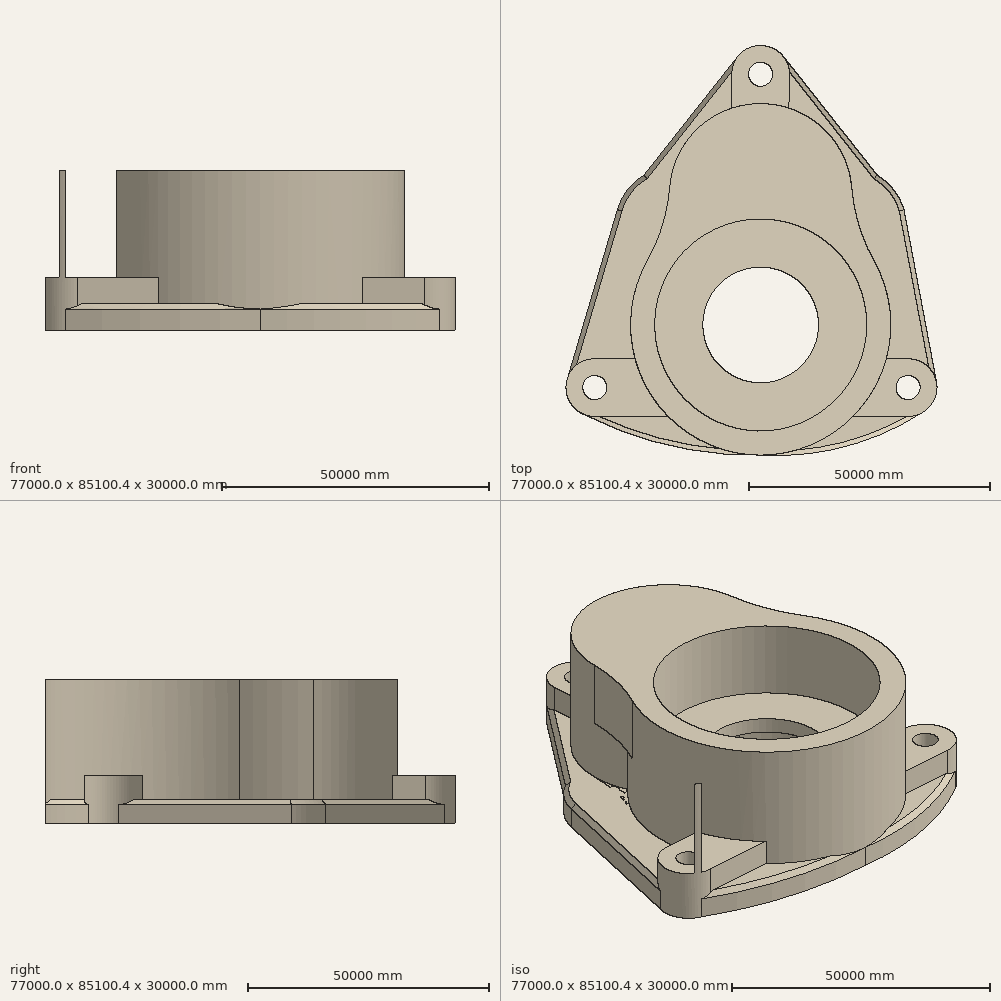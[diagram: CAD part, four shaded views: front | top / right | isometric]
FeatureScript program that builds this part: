
annotation { "Feature Type Name" : "Feature", "Feature Type Description" : "" }
export const myFeature = defineFeature(function(context is Context, id is Id, definition is map)
    precondition{}
    {
        {
            var Q0;
            Q0=qCreatedBy(makeId("Top.planeOp"),FACE);
            var sketch = newSketch(context, id + "F0", { "sketchPlane" : qUnion([Q0])});
            skCircle(sketch, "E0", {"center": v(0, 0) * mm, "radius": 27000 * mm});
            skCircle(sketch, "E1", {"center": v(0, 0) * mm, "radius": 22000 * mm});
            skCircle(sketch, "E2", {"center": v(0, 0) * mm, "radius": 12000 * mm});
            skCircle(sketch, "E3", {"center": v(0, 27000) * mm, "radius": 13939.8 * mm});
            skArc(sketch, "E4", {"start": v(17736.64, 20357.1) * mm, "mid": v(0, 45939.8) * mm, "end": v(-17736.64, 20357.1) * mm});
            skCircle(sketch, "E5", {"center": v(0, 52000) * mm, "radius": 6000 * mm});
            skCircle(sketch, "E6", {"center": v(0, 52000) * mm, "radius": 2500 * mm});
            skLineSegment(sketch, "E7", {"start": v(-5996.4, 52208) * mm, "end": v(-5996.4, 44965.51) * mm});
            skLineSegment(sketch, "E8", {"start": v(5998.36, 51859.79) * mm, "end": v(5838.42, 45017.47) * mm});
            skCircle(sketch, "E9", {"center": v(-34415.2, -13000) * mm, "radius": 2500 * mm});
            skCircle(sketch, "E10", {"center": v(30584.8, -13000) * mm, "radius": 2500 * mm});
            skCircle(sketch, "E11", {"center": v(-34415.2, -13000) * mm, "radius": 6000 * mm});
            skCircle(sketch, "E12", {"center": v(30584.8, -13000) * mm, "radius": 6000 * mm});
            skLineSegment(sketch, "E13", {"start": v(-34341.66, -18999.55) * mm, "end": v(-19183.77, -18999.55) * mm});
            skLineSegment(sketch, "E14", {"start": v(-34415.2, -7000) * mm, "end": v(-26076.8, -7000) * mm});
            skLineSegment(sketch, "E15", {"start": v(30695.67, -18998.98) * mm, "end": v(19184.34, -18998.98) * mm});
            skLineSegment(sketch, "E16", {"start": v(30584.8, -7000) * mm, "end": v(26076.8, -7000) * mm});
            skPoint(sketch, "E17", {"position": v(-28142.5, 27000) * mm});
            skPoint(sketch, "E18", {"position": v(28142.5, 27000) * mm});
            skArc(sketch, "E19", {"start": v(-24201.45, 31055.53) * mm, "mid": v(-27631.17, 27995.7) * mm, "end": v(-29723.12, 23903.13) * mm});
            skArc(sketch, "E20", {"start": v(30190.87, 21425.74) * mm, "mid": v(28351.05, 26958.94) * mm, "end": v(24201.45, 31055.53) * mm});
            skLineSegment(sketch, "E21", {"start": v(-39967.73, -10726.37) * mm, "end": v(-29723.12, 23903.13) * mm});
            skLineSegment(sketch, "E22", {"start": v(-24201.45, 31055.53) * mm, "end": v(-4707.26, 55720.44) * mm});
            skLineSegment(sketch, "E23", {"start": v(36480.63, -11886.8) * mm, "end": v(29723.12, 23903.13) * mm});
            skLineSegment(sketch, "E24", {"start": v(24201.45, 31055.53) * mm, "end": v(4707.26, 55720.44) * mm});
            skArc(sketch, "E25", {"start": v(-37734.14, -17998.46) * mm, "mid": v(-19439.08, -24897.08) * mm, "end": v(0, -27000) * mm});
            skArc(sketch, "E26", {"start": v(0, -27000) * mm, "mid": v(17495.5, -25276.65) * mm, "end": v(33586.38, -18195.24) * mm});
            skPoint(sketch, "E27.orphan", {"position": v(-40311.03, -11886.8) * mm});
            skSolve(sketch);
        }
        {
            var Q0;
            {var subQ0=sQuery(id+"F0.wireOp",EDGE,"E25");var subQ1=sQuery(id+"F0.wireOp",EDGE,"E11");var subQ2=makeQuery(id+"F0.imprint","INTERSECT",VERTEX,{"disambiguationData":[OD(0.0)],"derivedFrom":[subQ1,subQ0]});Q0=makeQuery(id+"F0.imprint","IMPRINT",FACE,{"disambiguationData":[TD([[makeQuery(id+"F0.imprint","IMPRINT",EDGE,{"disambiguationData":[TD([[subQ2,-1.0]])],"derivedFrom":subQ1}),1.0]])]});}
            var Q1;
            {var subQ0=sQuery(id+"F0.wireOp",EDGE,"E23");var subQ1=sQuery(id+"F0.wireOp",EDGE,"E20");var subQ2=makeQuery(id+"F0.imprint","INTERSECT",VERTEX,{"disambiguationData":[OD(0.0)],"derivedFrom":[subQ1,subQ0]});Q1=makeQuery(id+"F0.imprint","IMPRINT",FACE,{"disambiguationData":[TD([[makeQuery(id+"F0.imprint","IMPRINT",EDGE,{"disambiguationData":[TD([[subQ2,-1.0]])],"derivedFrom":subQ1}),1.0]])]});}
            var Q2;
            {var subQ0=sQuery(id+"F0.wireOp",EDGE,"E4");var subQ1=sQuery(id+"F0.wireOp",EDGE,"E0");var subQ2=makeQuery(id+"F0.imprint","INTERSECT",VERTEX,{"disambiguationData":[OD(0.0)],"derivedFrom":[subQ1,subQ0]});Q2=makeQuery(id+"F0.imprint","IMPRINT",FACE,{"disambiguationData":[TD([[makeQuery(id+"F0.imprint","IMPRINT",EDGE,{"disambiguationData":[TD([[subQ2,-1.0]])],"derivedFrom":subQ1}),-1.0]])]});}
            var Q3;
            {var subQ0=sQuery(id+"F0.wireOp",EDGE,"E3");var subQ1=sQuery(id+"F0.wireOp",EDGE,"E0");var subQ2=makeQuery(id+"F0.imprint","INTERSECT",VERTEX,{"disambiguationData":[OD(0.0)],"derivedFrom":[subQ1,subQ0]});Q3=makeQuery(id+"F0.imprint","IMPRINT",FACE,{"disambiguationData":[TD([[makeQuery(id+"F0.imprint","IMPRINT",EDGE,{"disambiguationData":[TD([[subQ2,-1.0]])],"derivedFrom":subQ1}),-1.0]])]});}
            var Q4;
            {var subQ0=sQuery(id+"F0.wireOp",EDGE,"E3");var subQ1=sQuery(id+"F0.wireOp",EDGE,"E0");var subQ2=makeQuery(id+"F0.imprint","INTERSECT",VERTEX,{"disambiguationData":[OD(0.0)],"derivedFrom":[subQ1,subQ0]});Q4=makeQuery(id+"F0.imprint","IMPRINT",FACE,{"disambiguationData":[TD([[makeQuery(id+"F0.imprint","IMPRINT",EDGE,{"disambiguationData":[TD([[subQ2,-1.0]])],"derivedFrom":subQ1}),1.0]])]});}
            var Q5;
            {var subQ0=sQuery(id+"F0.wireOp",EDGE,"E3");var subQ1=sQuery(id+"F0.wireOp",EDGE,"E1");var subQ2=makeQuery(id+"F0.imprint","INTERSECT",VERTEX,{"disambiguationData":[OD(0.0)],"derivedFrom":[subQ1,subQ0]});Q5=makeQuery(id+"F0.imprint","IMPRINT",FACE,{"disambiguationData":[TD([[makeQuery(id+"F0.imprint","IMPRINT",EDGE,{"disambiguationData":[TD([[subQ2,1.0]])],"derivedFrom":subQ1}),1.0]])]});}
            var Q6;
            {var subQ1=sQuery(id+"F0.wireOp",EDGE,"E0");var subQ6=sQuery(id+"F0.wireOp",EDGE,"E4");var subQ7=makeQuery(id+"F0.imprint","INTERSECT",VERTEX,{"disambiguationData":[OD(0.0)],"derivedFrom":[subQ1,subQ6]});Q6=makeQuery(id+"F0.imprint","IMPRINT",FACE,{"disambiguationData":[TD([[makeQuery(id+"F0.imprint","IMPRINT",EDGE,{"disambiguationData":[TD([[subQ7,-1.0]])],"derivedFrom":subQ1}),1.0]])]});}
            var Q7;
            Q7=makeQuery(id+"F0.imprint","IMPRINT",FACE,{"disambiguationData":[TD([[makeQuery(id+"F0.imprint","IMPRINT",EDGE,{"derivedFrom":sQuery(id+"F0.wireOp",EDGE,"E2")}),1.0]])]});
            var Q8;
            Q8=makeQuery(id+"F0.imprint","IMPRINT",FACE,{"disambiguationData":[TD([[makeQuery(id+"F0.imprint","IMPRINT",EDGE,{"derivedFrom":sQuery(id+"F0.wireOp",EDGE,"E2")}),-1.0]])]});
            extrude(context, id + "F1", {"entities" : qUnion([Q0, Q1, Q2, Q3, Q4, Q5, Q6, Q7, Q8]), "depth" : 30000 * mm});
        }
        {
            var Q0;
            {var subQ0=sQuery(id+"F0.wireOp",EDGE,"E4");var subQ1=sQuery(id+"F0.wireOp",EDGE,"E0");Q0=makeQuery(id+"F1.opExtrude","SWEPT_EDGE",EDGE,{"disambiguationData":[OSD([subQ1,subQ0]),TDD([makeQuery(id+"F0.imprint","INTERSECT",VERTEX,{"disambiguationData":[OD(0.0)],"derivedFrom":[subQ1,subQ0]})])]});}
            var Q1;
            {var subQ0=sQuery(id+"F0.wireOp",EDGE,"E4");var subQ1=sQuery(id+"F0.wireOp",EDGE,"E0");Q1=makeQuery(id+"F1.opExtrude","SWEPT_EDGE",EDGE,{"disambiguationData":[OSD([subQ1,subQ0]),TDD([makeQuery(id+"F0.imprint","INTERSECT",VERTEX,{"disambiguationData":[OD(1.0)],"derivedFrom":[subQ1,subQ0]})])]});}
            fillet(context, id + "F2", {"entities" : qUnion([Q0, Q1]), "radius" : 37817.8 * mm, "tangentPropagation" : true, "allowEdgeOverflow" : false});
        }
        {
            var Q0;
            Q0=makeQuery(id+"F0.imprint","IMPRINT",FACE,{"disambiguationData":[TD([[makeQuery(id+"F0.imprint","IMPRINT",EDGE,{"derivedFrom":sQuery(id+"F0.wireOp",EDGE,"E6")}),-1.0]])]});
            var Q1;
            {var subQ0=sQuery(id+"F0.wireOp",EDGE,"E7");var subQ1=sQuery(id+"F0.wireOp",EDGE,"E4");var subQ2=makeQuery(id+"F0.imprint","INTERSECT",VERTEX,{"derivedFrom":[subQ1,subQ0]});Q1=makeQuery(id+"F0.imprint","IMPRINT",FACE,{"disambiguationData":[TD([[makeQuery(id+"F0.imprint","IMPRINT",EDGE,{"disambiguationData":[TD([[subQ2,1.0]])],"derivedFrom":subQ1}),-1.0]])]});}
            var Q2;
            {var subQ0=sQuery(id+"F0.wireOp",EDGE,"E8");Q2=makeQuery(id+"F0.imprint","IMPRINT",FACE,{"disambiguationData":[TD([[makeQuery(id+"F0.imprint","IMPRINT",EDGE,{"derivedFrom":subQ0}),-1.0]])]});}
            var Q3;
            {var subQ3=sQuery(id+"F0.wireOp",EDGE,"E16");Q3=makeQuery(id+"F0.imprint","IMPRINT",FACE,{"disambiguationData":[TD([[makeQuery(id+"F0.imprint","IMPRINT",EDGE,{"derivedFrom":subQ3}),1.0]])]});}
            var Q4;
            Q4=makeQuery(id+"F0.imprint","IMPRINT",FACE,{"disambiguationData":[TD([[makeQuery(id+"F0.imprint","IMPRINT",EDGE,{"derivedFrom":sQuery(id+"F0.wireOp",EDGE,"E10")}),-1.0]])]});
            var Q5;
            Q5=makeQuery(id+"F0.imprint","IMPRINT",FACE,{"disambiguationData":[TD([[makeQuery(id+"F0.imprint","IMPRINT",EDGE,{"derivedFrom":sQuery(id+"F0.wireOp",EDGE,"E9")}),-1.0]])]});
            var Q6;
            {var subQ0=sQuery(id+"F0.wireOp",EDGE,"E13");Q6=makeQuery(id+"F0.imprint","IMPRINT",FACE,{"disambiguationData":[TD([[makeQuery(id+"F0.imprint","IMPRINT",EDGE,{"derivedFrom":subQ0}),1.0]])]});}
            extrude(context, id + "F3", {"entities" : qUnion([Q0, Q1, Q2, Q3, Q4, Q5, Q6]), "operationType" : NewBodyOperationType.ADD, "depth" : 10000 * mm});
        }
        {
            var Q0;
            {var subQ5=sQuery(id+"F0.wireOp",EDGE,"E14");Q0=makeQuery(id+"F0.imprint","IMPRINT",FACE,{"disambiguationData":[TD([[makeQuery(id+"F0.imprint","IMPRINT",EDGE,{"derivedFrom":subQ5}),1.0]])]});}
            var Q1;
            {var subQ0=sQuery(id+"F0.wireOp",EDGE,"E8");Q1=makeQuery(id+"F0.imprint","IMPRINT",FACE,{"disambiguationData":[TD([[makeQuery(id+"F0.imprint","IMPRINT",EDGE,{"derivedFrom":subQ0}),1.0]])]});}
            var Q2;
            {var subQ0=sQuery(id+"F0.wireOp",EDGE,"E13");Q2=makeQuery(id+"F0.imprint","IMPRINT",FACE,{"disambiguationData":[TD([[makeQuery(id+"F0.imprint","IMPRINT",EDGE,{"derivedFrom":subQ0}),-1.0]])]});}
            var Q3;
            {var subQ6=sQuery(id+"F0.wireOp",EDGE,"E26");Q3=makeQuery(id+"F0.imprint","IMPRINT",FACE,{"disambiguationData":[TD([[makeQuery(id+"F0.imprint","IMPRINT",EDGE,{"derivedFrom":subQ6}),1.0]])]});}
            extrude(context, id + "F4", {"entities" : qUnion([Q0, Q1, Q2, Q3]), "depth" : 5000 * mm});
        }
        {
            var Q0;
            {var subQ0=sQuery(id+"F0.wireOp",EDGE,"E3");var subQ1=sQuery(id+"F0.wireOp",EDGE,"E0");var subQ2=makeQuery(id+"F0.imprint","INTERSECT",VERTEX,{"disambiguationData":[OD(0.0)],"derivedFrom":[subQ1,subQ0]});Q0=makeQuery(id+"F0.imprint","IMPRINT",FACE,{"disambiguationData":[TD([[makeQuery(id+"F0.imprint","IMPRINT",EDGE,{"disambiguationData":[TD([[subQ2,-1.0]])],"derivedFrom":subQ1}),-1.0]])]});}
            var Q1;
            {var subQ0=sQuery(id+"F0.wireOp",EDGE,"E3");var subQ1=sQuery(id+"F0.wireOp",EDGE,"E0");var subQ2=makeQuery(id+"F0.imprint","INTERSECT",VERTEX,{"disambiguationData":[OD(0.0)],"derivedFrom":[subQ1,subQ0]});Q1=makeQuery(id+"F0.imprint","IMPRINT",FACE,{"disambiguationData":[TD([[makeQuery(id+"F0.imprint","IMPRINT",EDGE,{"disambiguationData":[TD([[subQ2,-1.0]])],"derivedFrom":subQ1}),1.0]])]});}
            var Q2;
            {var subQ0=sQuery(id+"F0.wireOp",EDGE,"E3");var subQ1=sQuery(id+"F0.wireOp",EDGE,"E1");var subQ2=makeQuery(id+"F0.imprint","INTERSECT",VERTEX,{"disambiguationData":[OD(0.0)],"derivedFrom":[subQ1,subQ0]});Q2=makeQuery(id+"F0.imprint","IMPRINT",FACE,{"disambiguationData":[TD([[makeQuery(id+"F0.imprint","IMPRINT",EDGE,{"disambiguationData":[TD([[subQ2,1.0]])],"derivedFrom":subQ1}),1.0]])]});}
            var Q3;
            Q3=makeQuery(id+"F0.imprint","IMPRINT",FACE,{"disambiguationData":[TD([[makeQuery(id+"F0.imprint","IMPRINT",EDGE,{"derivedFrom":sQuery(id+"F0.wireOp",EDGE,"E2")}),-1.0]])]});
            var Q4;
            Q4=makeQuery(id+"F0.imprint","IMPRINT",FACE,{"disambiguationData":[TD([[makeQuery(id+"F0.imprint","IMPRINT",EDGE,{"derivedFrom":sQuery(id+"F0.wireOp",EDGE,"E2")}),1.0]])]});
            var Q5;
            Q5=makeQuery(id+"F4.opExtrude","CAP_FACE",FACE,{"disambiguationData":[OSD([sQuery(id+"F0.wireOp",EDGE,"E0"),sQuery(id+"F0.wireOp",EDGE,"E4"),sQuery(id+"F0.wireOp",EDGE,"E5"),sQuery(id+"F0.wireOp",EDGE,"E7"),sQuery(id+"F0.wireOp",EDGE,"E11"),sQuery(id+"F0.wireOp",EDGE,"E14"),sQuery(id+"F0.wireOp",EDGE,"E19"),sQuery(id+"F0.wireOp",EDGE,"E21"),sQuery(id+"F0.wireOp",EDGE,"E22")])],"isStart":false});
            extrude(context, id + "F5", {"entities" : qUnion([Q0, Q1, Q2, Q3, Q4, Q5]), "operationType" : NewBodyOperationType.REMOVE, "depth" : 12000 * mm});
        }
        {
            var Q0;
            Q0=makeQuery(id+"F1.opExtrude","CAP_FACE",FACE,{"disambiguationData":[OSD([sQuery(id+"F0.wireOp",EDGE,"E0"),sQuery(id+"F0.wireOp",EDGE,"E4")])],"isStart":false});
            var sketch = newSketch(context, id + "F6", { "sketchPlane" : qUnion([Q0])});
            skCircle(sketch, "E28.0", {"center": v(0, 0) * mm, "radius": 22000 * mm});
            skSolve(sketch);
        }
        {
            var Q0;
            Q0=qSketchRegion(id+"F6",true);
            extrude(context, id + "F7", {"entities" : qUnion([Q0]), "operationType" : NewBodyOperationType.REMOVE, "oppositeDirection" : true, "depth" : 15000 * mm});
        }
        {
            var Q0;
            Q0=makeQuery(id+"F0.imprint","IMPRINT",FACE,{"disambiguationData":[TD([[makeQuery(id+"F0.imprint","IMPRINT",EDGE,{"derivedFrom":sQuery(id+"F0.wireOp",EDGE,"E2")}),1.0]])]});
            extrude(context, id + "F8", {"entities" : qUnion([Q0]), "operationType" : NewBodyOperationType.REMOVE, "endBound" : BoundingType.THROUGH_ALL, "depth" : 25 * mm});
        }
        {
            var Q0;
            Q0=makeQuery(id+"F1.opExtrude","SWEPT_BODY",BODY,{"disambiguationData":[OSD([sQuery(id+"F0.wireOp",EDGE,"E11"),sQuery(id+"F0.wireOp",EDGE,"E25")])]});
            var Q1;
            Q1=makeQuery(id+"F1.opExtrude","SWEPT_BODY",BODY,{"disambiguationData":[OSD([sQuery(id+"F0.wireOp",EDGE,"E20"),sQuery(id+"F0.wireOp",EDGE,"E23")])]});
            deleteBodies(context, id + "F9", {"entities" : qUnion([Q0, Q1])});
        }
        {
            var Q0;
            Q0=makeQuery(id+"F1.opExtrude","CAP_EDGE",EDGE,{"disambiguationData":[OSD([sQuery(id+"F0.wireOp",EDGE,"E4")])],"isStart":false});
            var Q1;
            {var subQ0=sQuery(id+"F0.wireOp",EDGE,"E4");var subQ1=sQuery(id+"F0.wireOp",EDGE,"E0");Q1=makeQuery(id+"F2.opFillet","BLEND_EDGE",EDGE,{"blendedFrom":[makeQuery(id+"F1.opExtrude","SWEPT_EDGE",EDGE,{"disambiguationData":[OSD([subQ1,subQ0]),TDD([makeQuery(id+"F0.imprint","INTERSECT",VERTEX,{"disambiguationData":[OD(0.0)],"derivedFrom":[subQ1,subQ0]})])]}),makeQuery(id+"F1.opExtrude","CAP_FACE",FACE,{"disambiguationData":[OSD([subQ1,subQ0])],"isStart":false})],"blendedInto":[makeQuery(id+"F1.opExtrude","CAP_FACE",FACE,{"disambiguationData":[OSD([subQ1,subQ0])],"isStart":false})]});}
            var Q2;
            Q2=makeQuery(id+"F4.opExtrude","CAP_EDGE",EDGE,{"disambiguationData":[OSD([sQuery(id+"F0.wireOp",EDGE,"E22")])],"isStart":false});
            var Q3;
            Q3=makeQuery(id+"F4.opExtrude","CAP_EDGE",EDGE,{"disambiguationData":[OSD([sQuery(id+"F0.wireOp",EDGE,"E19")])],"isStart":false});
            var Q4;
            Q4=makeQuery(id+"F4.opExtrude","CAP_EDGE",EDGE,{"disambiguationData":[OSD([sQuery(id+"F0.wireOp",EDGE,"E21")])],"isStart":false});
            var Q5;
            Q5=makeQuery(id+"F4.opExtrude","CAP_EDGE",EDGE,{"disambiguationData":[OSD([sQuery(id+"F0.wireOp",EDGE,"E23")])],"isStart":false});
            var Q6;
            Q6=makeQuery(id+"F4.opExtrude","CAP_EDGE",EDGE,{"disambiguationData":[OSD([sQuery(id+"F0.wireOp",EDGE,"E24")])],"isStart":false});
            var Q7;
            Q7=makeQuery(id+"F4.opExtrude","CAP_EDGE",EDGE,{"disambiguationData":[OSD([sQuery(id+"F0.wireOp",EDGE,"E20")])],"isStart":false});
            var Q8;
            Q8=makeQuery(id+"F3.opExtrude","CAP_FACE",FACE,{"disambiguationData":[OSD([sQuery(id+"F0.wireOp",EDGE,"E0"),sQuery(id+"F0.wireOp",EDGE,"E10"),sQuery(id+"F0.wireOp",EDGE,"E12"),sQuery(id+"F0.wireOp",EDGE,"E15"),sQuery(id+"F0.wireOp",EDGE,"E16")])],"isStart":false});
            var Q9;
            Q9=makeQuery(id+"F3.opExtrude","CAP_FACE",FACE,{"disambiguationData":[OSD([sQuery(id+"F0.wireOp",EDGE,"E0"),sQuery(id+"F0.wireOp",EDGE,"E9"),sQuery(id+"F0.wireOp",EDGE,"E11"),sQuery(id+"F0.wireOp",EDGE,"E13"),sQuery(id+"F0.wireOp",EDGE,"E14"),sQuery(id+"F0.wireOp",EDGE,"E25")])],"isStart":false});
            chamfer(context, id + "F10", {"entities" : qUnion([Q0, Q1, Q2, Q3, Q4, Q5, Q6, Q7, Q8, Q9]), "width" : 1000 * mm, "tangentPropagation" : true});
        }
        {
            var Q0;
            Q0=makeQuery(id+"F4.opExtrude","CAP_EDGE",EDGE,{"disambiguationData":[OSD([sQuery(id+"F0.wireOp",EDGE,"E25")])],"isStart":false});
            var Q1;
            Q1=makeQuery(id+"F4.opExtrude","CAP_EDGE",EDGE,{"disambiguationData":[OSD([sQuery(id+"F0.wireOp",EDGE,"E26")])],"isStart":false});
            chamfer(context, id + "F11", {"entities" : qUnion([Q0, Q1]), "width" : 1000 * mm, "tangentPropagation" : true});
        }
    });
